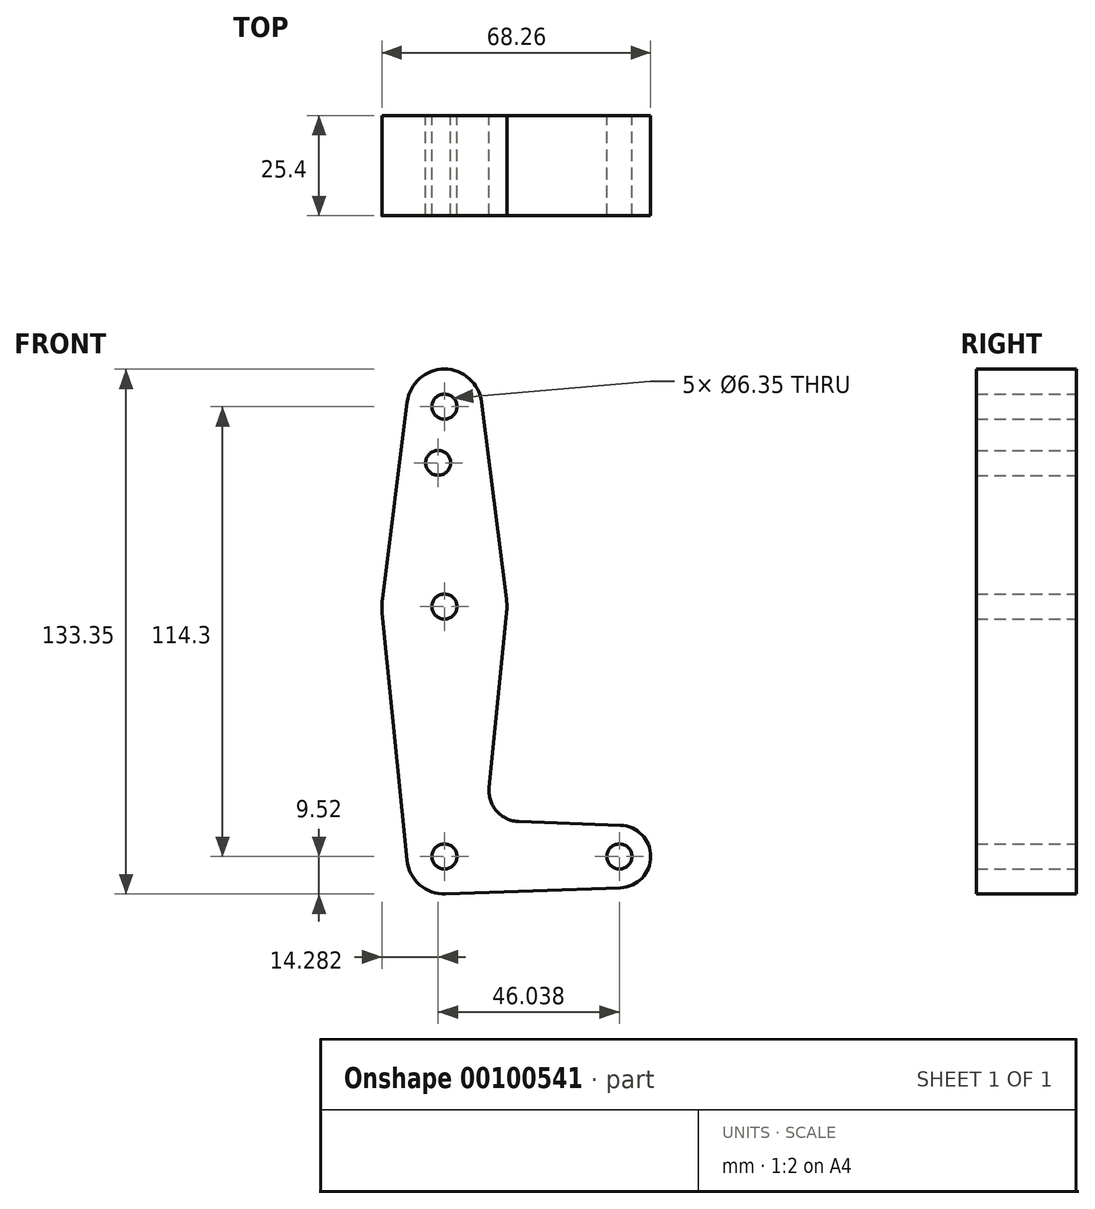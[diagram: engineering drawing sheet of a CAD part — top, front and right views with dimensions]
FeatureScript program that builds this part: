
annotation { "Feature Type Name" : "Feature", "Feature Type Description" : "" }
export const myFeature = defineFeature(function(context is Context, id is Id, definition is map)
    precondition{}
    {
        {
            var Q0;
            Q0=qCreatedBy(makeId("Front.planeOp"),FACE);
            var sketch = newSketch(context, id + "F0", { "sketchPlane" : qUnion([Q0])});
            skLineSegment(sketch, "E0", {"start": v(0, 0) * mm, "end": v(0, 114.3) * mm, "construction": true});
            skLineSegment(sketch, "E1", {"start": v(0, 0) * mm, "end": v(44.45, 0) * mm, "construction": true});
            skCircle(sketch, "E2", {"center": v(0, 114.3) * mm, "radius": 9.53 * mm});
            skCircle(sketch, "E3", {"center": v(0, 63.5) * mm, "radius": 15.88 * mm});
            skCircle(sketch, "E4", {"center": v(0, 0) * mm, "radius": 9.53 * mm});
            skCircle(sketch, "E5", {"center": v(44.45, 0) * mm, "radius": 7.94 * mm});
            skLineSegment(sketch, "E6", {"start": v(-9.45, 115.5) * mm, "end": v(-15.75, 65.48) * mm});
            skLineSegment(sketch, "E7", {"start": v(9.45, 115.5) * mm, "end": v(15.75, 65.48) * mm});
            skLineSegment(sketch, "E8", {"start": v(-15.8, 61.91) * mm, "end": v(-9.48, -0.95) * mm});
            skLineSegment(sketch, "E9", {"start": v(15.8, 61.91) * mm, "end": v(11.34, 17.6) * mm});
            skLineSegment(sketch, "E10", {"start": v(18.97, 8.85) * mm, "end": v(44.73, 7.93) * mm});
            skLineSegment(sketch, "E11", {"start": v(0.34, -9.52) * mm, "end": v(44.73, -7.93) * mm});
            skCircle(sketch, "E12", {"center": v(0, 114.3) * mm, "radius": 3.18 * mm});
            skCircle(sketch, "E13", {"center": v(0, 63.5) * mm, "radius": 3.18 * mm});
            skCircle(sketch, "E14", {"center": v(0, 0) * mm, "radius": 3.18 * mm});
            skCircle(sketch, "E15", {"center": v(44.45, 0) * mm, "radius": 3.18 * mm});
            skCircle(sketch, "E16", {"center": v(-1.59, 100.03) * mm, "radius": 3.18 * mm});
            skArc(sketch, "E17.filletArc", {"start": v(11.34, 17.6) * mm, "mid": v(13.26, 11.57) * mm, "end": v(18.97, 8.85) * mm});
            skSolve(sketch);
        }
        {
            var Q0;
            Q0 = qSketchRegion(id + "F0", true);
            extrude(context, id + "F1", {"entities" : qUnion([Q0]), "depth" : 25.4 * mm});
        }
    });
